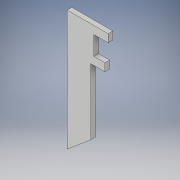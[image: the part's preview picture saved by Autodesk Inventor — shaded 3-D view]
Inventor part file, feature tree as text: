
AUTODESK INVENTOR PART (.ipt)
format: ipt  version: 2017 (Build 210142000, 142)  size: 114,688 bytes
history: native  units: in
note: dims shown in document units (in); Inventor stores cm internally (conversion verified against a paired STEP export)
features: extrude x1, sketch x1
ambient origin geometry x8: Origin, YZ Plane, XZ Plane, XY Plane, X Axis, Y Axis, Z Axis, Center Point
bodies: Body1 (feature_tree)
feature tree (2):
  extrude  "Extrusion1"  Depth=0.0787in
  sketch  "Sketch2"  dims[d9=0.1181in d10=0.0in d17=0.0787in d18=0.2756in d19=0.3543in d20=0.1969in d21=0.1969in d22=0.5906in d23=0.4724in d24=0.0787in d25=1.8474in d26=0.8933in]
